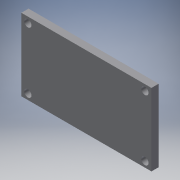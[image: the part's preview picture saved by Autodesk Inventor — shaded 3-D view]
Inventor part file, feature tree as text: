
AUTODESK INVENTOR PART (.ipt)
format: ipt  version: 2018.3 (Build 223284000, 284)  size: 180,224 bytes
history: native  units: mm
features: other x3, sketch x3, extrude x2, chamfer x1, hole x1
ambient origin geometry x8: Origin, YZ Plane, XZ Plane, XY Plane, X Axis, Y Axis, Z Axis, Center Point
bodies: Solid1 (feature_tree)
feature tree (10):
  other  "Annotations"
  extrude  "Extrusion1"  Depth=5.0mm
  extrude  "Extrusion2"  Depth=50.0mm
  chamfer  "Chamfer1"  Distance=18.0mm
  hole  "Hole2"  [1 undecoded]
  sketch  "Sketch1"  dims[d0=90.0mm d1=5.0mm]
  sketch  "Sketch2"  dims[d2=50.0mm d3=0.0mm d4=20.0mm]
  sketch  "Sketch3"  dims[d5=14.0mm d6=18.0mm d7=18.0mm d8=35.0mm d9=35.0mm d11=1.13mm d12=1.45mm d13=1.45mm d15=1.13mm d16=1.13mm d17=1.1mm d18=1.1mm d19=1.13mm d28=2.15mm d29=2.15mm d30=4.83298mm d31=2.15mm d32=2.15mm d33=4.83298mm d34=4.5mm d35=0.0mm d36=0.5mm d37=2.0mm d38=45.0deg d46=4.5mm d47=4.5mm d48=4.0mm d49=4.0mm d50=5.0mm d51=6.0mm d52=4.0mm d53=2.0mm d54=90.0deg d55=8.0mm d56=20.594885mm d57=4.5mm d58=4.5mm d59=4.0mm d60=4.0mm d61=4.042715mm d62=35.542215mm d63=4.434539mm d64=35.542215mm]
  other  "Linear Dimension 1"
  other  "Linear Dimension 2"
note: 1 required parameter value undecoded (feature->parameter linkage not recoverable at this tier; creation-order binding heuristic only, values carry confidence <= 0.55)
